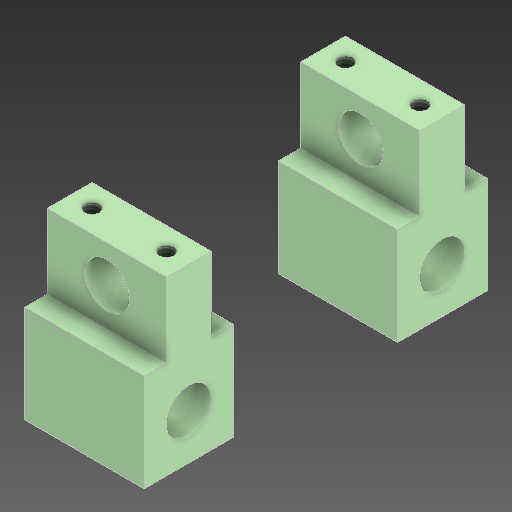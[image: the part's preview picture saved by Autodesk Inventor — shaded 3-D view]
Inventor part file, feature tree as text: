
AUTODESK INVENTOR PART (.ipt)
format: ipt  version: 2020 (Build 240168000, 168)  size: 191,488 bytes
history: native  units: mm
features: other x5, extrude x1, sketch x1, projected_geometry x1
ambient origin geometry x8: Origin, YZ Plane, XZ Plane, XY Plane, X Axis, Y Axis, Z Axis, Center Point
bodies: Body1 (feature_tree)
feature tree (8):
  other  "Bearing1.ipt"
  extrude  "擠出1"  Depth=110.0mm
  other  "實體1::Bearing1.ipt"
  other  "標籤特徵1"
  sketch  "草圖1"
  projected_geometry  "投影迴路1"
  other  "實體1"
  other  "投影切割邊1"
